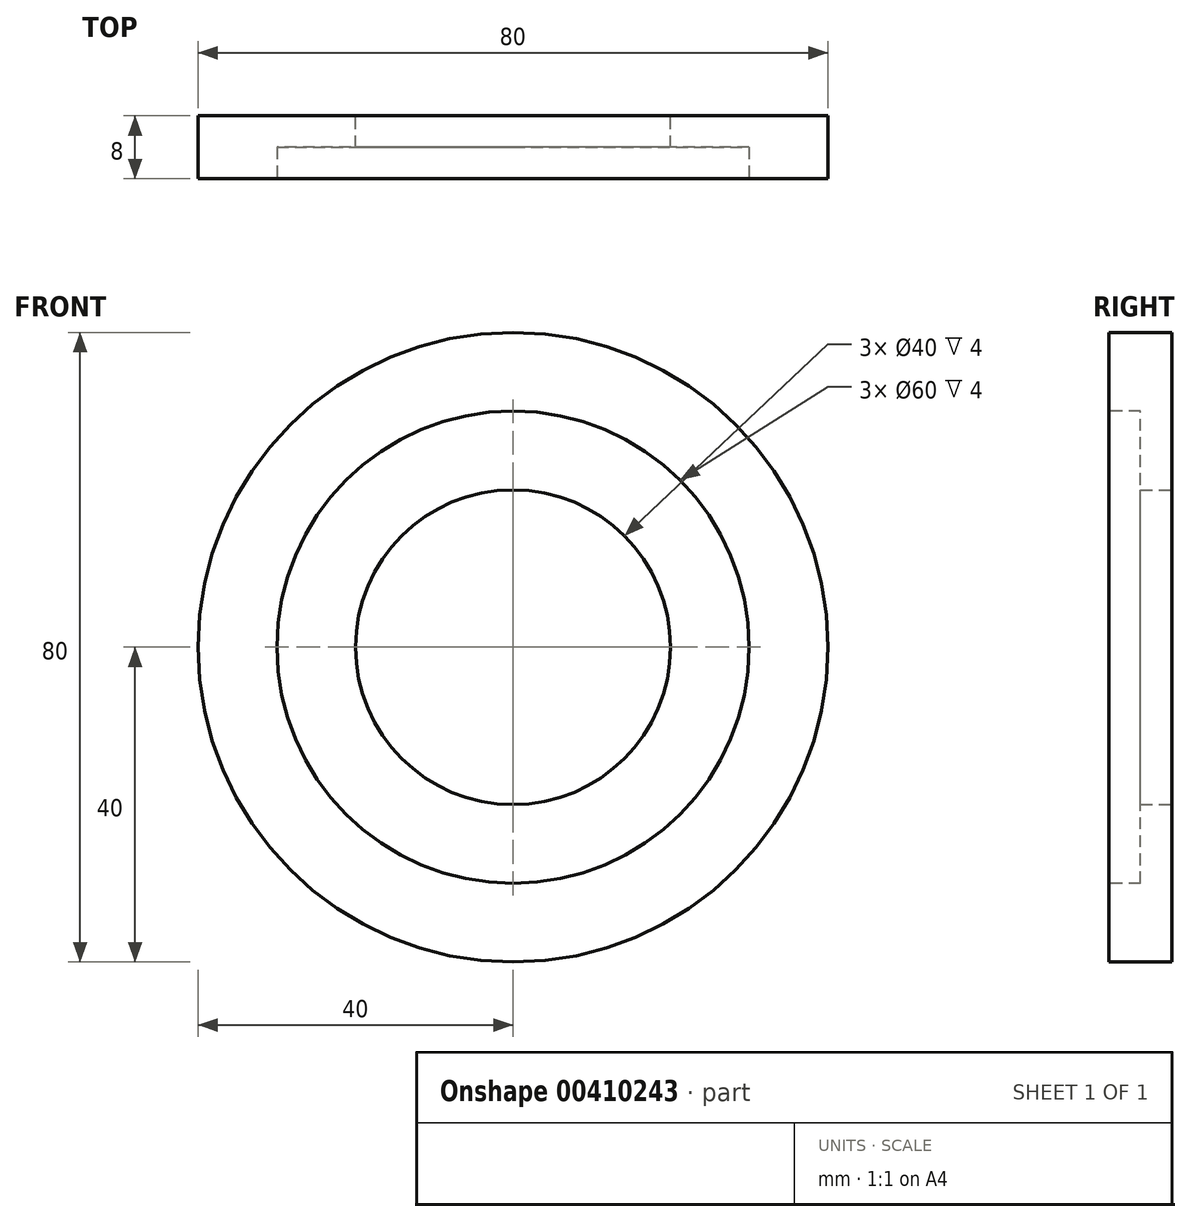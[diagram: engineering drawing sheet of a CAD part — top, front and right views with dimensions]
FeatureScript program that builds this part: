
annotation { "Feature Type Name" : "Feature", "Feature Type Description" : "" }
export const myFeature = defineFeature(function(context is Context, id is Id, definition is map)
    precondition{}
    {
        {
            var Q0;
            Q0=qCreatedBy(makeId("Front.planeOp"),FACE);
            var sketch = newSketch(context, id + "F0", { "sketchPlane" : qUnion([Q0])});
            skCircle(sketch, "E0", {"center": v(0, 0) * mm, "radius": 40 * mm});
            skCircle(sketch, "E1", {"center": v(0, 0) * mm, "radius": 20 * mm});
            skSolve(sketch);
        }
        {
            var Q0;
            Q0=makeQuery(id+"F0.imprint","IMPRINT",FACE,{"disambiguationData":[TD([[makeQuery(id+"F0.imprint","IMPRINT",EDGE,{"derivedFrom":sQuery(id+"F0.wireOp",EDGE,"E0")}),1.0]])]});
            extrude(context, id + "F1", {"entities" : qUnion([Q0]), "depth" : 8 * mm});
        }
        {
            var Q0;
            Q0=makeQuery(id+"F1.opExtrude","CAP_FACE",FACE,{"disambiguationData":[OSD([sQuery(id+"F0.wireOp",EDGE,"E0"),sQuery(id+"F0.wireOp",EDGE,"E1")])],"isStart":false});
            var sketch = newSketch(context, id + "F2", { "sketchPlane" : qUnion([Q0])});
            skCircle(sketch, "E2.0", {"center": v(0, 0) * mm, "radius": 30 * mm});
            skCircle(sketch, "E3.0", {"center": v(0, 0) * mm, "radius": 20 * mm});
            skSolve(sketch);
        }
        {
            var Q0;
            Q0=makeQuery(id+"F2.imprint","IMPRINT",FACE,{"disambiguationData":[TD([[makeQuery(id+"F2.imprint","IMPRINT",EDGE,{"derivedFrom":sQuery(id+"F2.wireOp",EDGE,"E2.0")}),1.0]])]});
            extrude(context, id + "F3", {"entities" : qUnion([Q0]), "operationType" : NewBodyOperationType.REMOVE, "oppositeDirection" : true, "depth" : 4 * mm});
        }
    });
